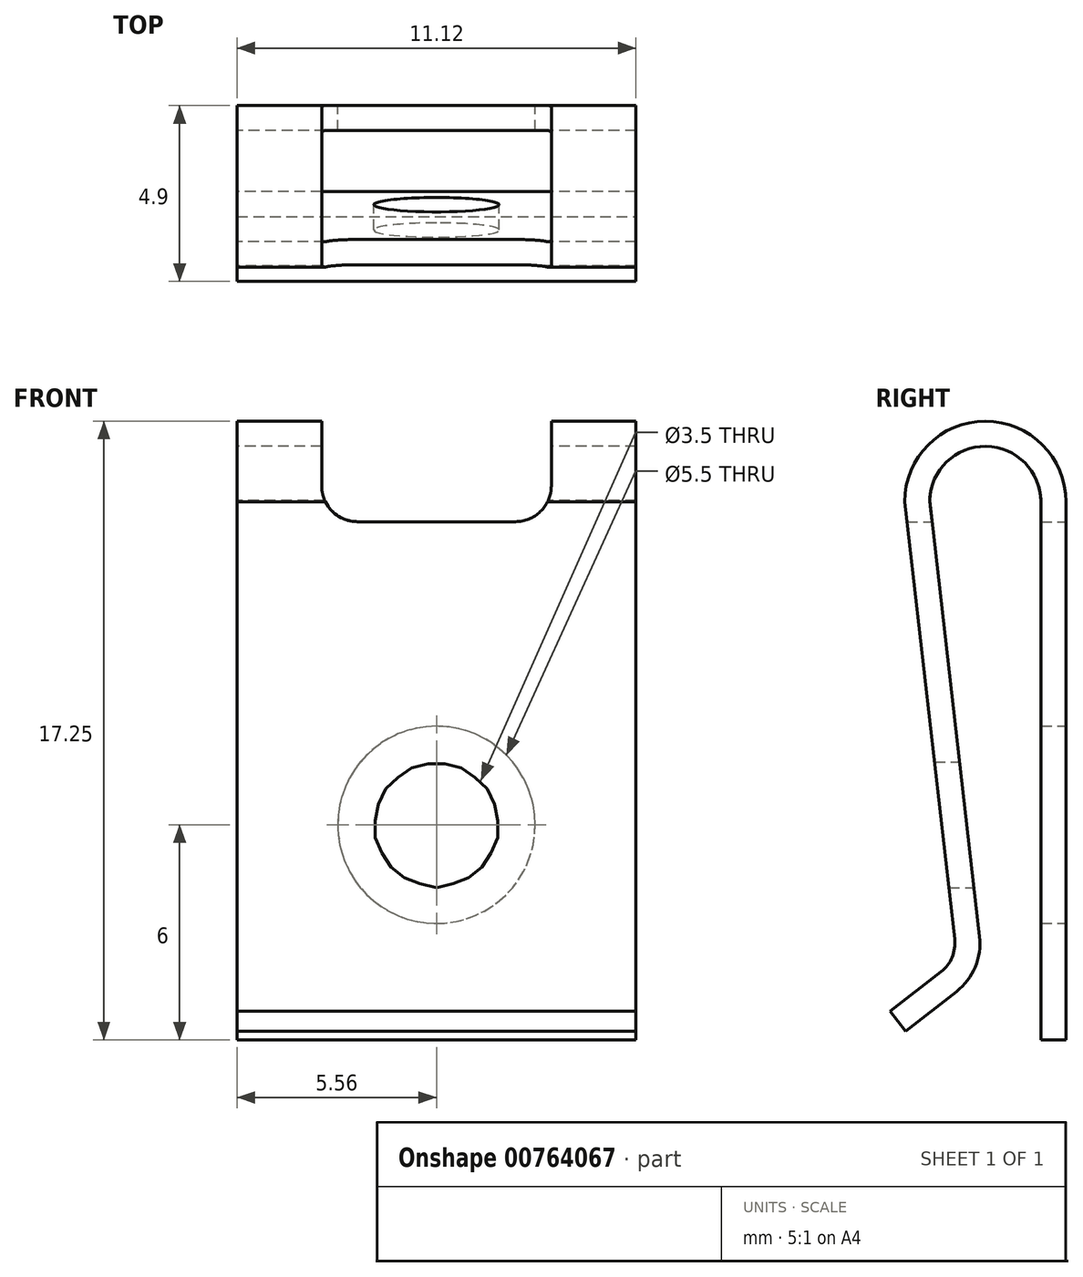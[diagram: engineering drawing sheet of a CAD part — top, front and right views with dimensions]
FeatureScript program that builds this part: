
annotation { "Feature Type Name" : "Feature", "Feature Type Description" : "" }
export const myFeature = defineFeature(function(context is Context, id is Id, definition is map)
    precondition{}
    {
        {
            var Q0;
            Q0=qCreatedBy(makeId("Right.planeOp"),FACE);
            var sketch = newSketch(context, id + "F0", { "sketchPlane" : qUnion([Q0])});
            skLineSegment(sketch, "E0", {"start": v(2.25, -15) * mm, "end": v(2.25, 0) * mm});
            skLineSegment(sketch, "E1", {"start": v(2.25, 0) * mm, "end": v(-2.25, 0) * mm, "construction": true});
            skLineSegment(sketch, "E2", {"start": v(-2.25, 0) * mm, "end": v(-0.8, -12.75) * mm});
            skLineSegment(sketch, "E3", {"start": v(-0.8, -12.75) * mm, "end": v(-2.65, -14.2) * mm});
            skArc(sketch, "E4", {"start": v(2.25, 0) * mm, "mid": v(0, 2.25) * mm, "end": v(-2.25, 0) * mm});
            skLineSegment(sketch, "E5.0", {"start": v(-0.05, -13.06) * mm, "end": v(-2.22, -14.75) * mm});
            skLineSegment(sketch, "E5.1", {"start": v(-1.55, 0.04) * mm, "end": v(-0.05, -13.06) * mm});
            skArc(sketch, "E5.2", {"start": v(1.55, 0) * mm, "mid": v(0.02, 1.55) * mm, "end": v(-1.55, 0.04) * mm});
            skLineSegment(sketch, "E5.3", {"start": v(1.55, -15) * mm, "end": v(1.55, 0) * mm});
            skLineSegment(sketch, "E6", {"start": v(-2.22, -14.75) * mm, "end": v(-2.65, -14.2) * mm});
            skLineSegment(sketch, "E7", {"start": v(2.25, -15) * mm, "end": v(1.55, -15) * mm});
            skSolve(sketch);
        }
        {
            var Q0;
            Q0=makeQuery(id+"F0.imprint","IMPRINT",FACE,{"disambiguationData":[TD([[makeQuery(id+"F0.imprint","IMPRINT",EDGE,{"derivedFrom":sQuery(id+"F0.wireOp",EDGE,"E0")}),1.0]])]});
            extrude(context, id + "F1", {"entities" : qUnion([Q0]), "endBound" : BoundingType.SYMMETRIC, "depth" : 11.12 * mm});
        }
        {
            var Q0;
            Q0=makeQuery(id+"F1.opExtrude","SWEPT_FACE",FACE,{"disambiguationData":[OSD([sQuery(id+"F0.wireOp",EDGE,"E0")])]});
            var sketch = newSketch(context, id + "F2", { "sketchPlane" : qUnion([Q0])});
            skLineSegment(sketch, "E8", {"start": v(0, -15) * mm, "end": v(0, -9) * mm, "construction": true});
            skCircle(sketch, "E9", {"center": v(0, -9) * mm, "radius": 2.75 * mm});
            skCircle(sketch, "E10", {"center": v(0, -9) * mm, "radius": 1.75 * mm});
            skLineSegment(sketch, "E11.bottom", {"start": v(-3.2, 3.95) * mm, "end": v(3.2, 3.95) * mm});
            skLineSegment(sketch, "E11.top", {"start": v(-3.2, -0.55) * mm, "end": v(3.2, -0.55) * mm});
            skLineSegment(sketch, "E11.left", {"start": v(-3.2, 3.95) * mm, "end": v(-3.2, -0.55) * mm});
            skLineSegment(sketch, "E11.right", {"start": v(3.2, 3.95) * mm, "end": v(3.2, -0.55) * mm});
            skSolve(sketch);
        }
        {
            var Q0;
            {var subQ0=sQuery(id+"F2.wireOp",EDGE,"E11.bottom");Q0=makeQuery(id+"F2.imprint","IMPRINT",FACE,{"disambiguationData":[TD([[makeQuery(id+"F2.imprint","IMPRINT",EDGE,{"derivedFrom":subQ0}),-1.0]])]});}
            var Q1;
            {var subQ0=sQuery(id+"F2.wireOp",EDGE,"E11.top");Q1=makeQuery(id+"F2.imprint","IMPRINT",FACE,{"disambiguationData":[TD([[makeQuery(id+"F2.imprint","IMPRINT",EDGE,{"derivedFrom":subQ0}),1.0]])]});}
            var Q2;
            Q2=makeQuery(id+"F2.imprint","IMPRINT",FACE,{"disambiguationData":[TD([[makeQuery(id+"F2.imprint","IMPRINT",EDGE,{"derivedFrom":sQuery(id+"F2.wireOp",EDGE,"E10")}),1.0]])]});
            extrude(context, id + "F3", {"entities" : qUnion([Q0, Q1, Q2]), "operationType" : NewBodyOperationType.REMOVE, "endBound" : BoundingType.THROUGH_ALL, "oppositeDirection" : true, "depth" : 25 * mm});
        }
        {
            var Q0;
            Q0=makeQuery(id+"F2.imprint","IMPRINT",FACE,{"disambiguationData":[TD([[makeQuery(id+"F2.imprint","IMPRINT",EDGE,{"derivedFrom":sQuery(id+"F2.wireOp",EDGE,"E9")}),1.0]])]});
            var Q1;
            Q1=makeQuery(id+"F1.opExtrude","SWEPT_FACE",FACE,{"disambiguationData":[OSD([sQuery(id+"F0.wireOp",EDGE,"E5.3")])]});
            extrude(context, id + "F4", {"entities" : qUnion([Q0]), "operationType" : NewBodyOperationType.REMOVE, "endBound" : BoundingType.UP_TO_SURFACE, "oppositeDirection" : true, "endBoundEntityFace" : qUnion([Q1]), "depth" : 25 * mm});
        }
        {
            var Q0;
            Q0=makeQuery(id+"F3.boolean.opBoolean","COPY",EDGE,{"disambiguationData":[OD(0.0)],"derivedFrom":makeQuery(id+"F3.opExtrude","SWEPT_EDGE",EDGE,{"disambiguationData":[OSD([sQuery(id+"F2.wireOp",EDGE,"E11.top"),sQuery(id+"F2.wireOp",EDGE,"E11.right")])]})});
            var Q1;
            Q1=makeQuery(id+"F3.boolean.opBoolean","COPY",EDGE,{"disambiguationData":[OD(1.0)],"derivedFrom":makeQuery(id+"F3.opExtrude","SWEPT_EDGE",EDGE,{"disambiguationData":[OSD([sQuery(id+"F2.wireOp",EDGE,"E11.top"),sQuery(id+"F2.wireOp",EDGE,"E11.right")])]})});
            var Q2;
            Q2=makeQuery(id+"F3.boolean.opBoolean","COPY",EDGE,{"disambiguationData":[OD(0.0)],"derivedFrom":makeQuery(id+"F3.opExtrude","SWEPT_EDGE",EDGE,{"disambiguationData":[OSD([sQuery(id+"F2.wireOp",EDGE,"E11.top"),sQuery(id+"F2.wireOp",EDGE,"E11.left")])]})});
            var Q3;
            Q3=makeQuery(id+"F3.boolean.opBoolean","COPY",EDGE,{"disambiguationData":[OD(1.0)],"derivedFrom":makeQuery(id+"F3.opExtrude","SWEPT_EDGE",EDGE,{"disambiguationData":[OSD([sQuery(id+"F2.wireOp",EDGE,"E11.top"),sQuery(id+"F2.wireOp",EDGE,"E11.left")])]})});
            var Q4;
            Q4=makeQuery(id+"F1.opExtrude","SWEPT_EDGE",EDGE,{"disambiguationData":[OSD([sQuery(id+"F0.wireOp",EDGE,"E2"),sQuery(id+"F0.wireOp",EDGE,"E3")])]});
            fillet(context, id + "F5", {"entities" : qUnion([Q0, Q1, Q2, Q3, Q4]), "radius" : 1 * mm, "tangentPropagation" : true, "allowEdgeOverflow" : false});
        }
        {
            var Q0;
            Q0=makeQuery(id+"F1.opExtrude","SWEPT_EDGE",EDGE,{"disambiguationData":[OSD([sQuery(id+"F0.wireOp",EDGE,"E5.0"),sQuery(id+"F0.wireOp",EDGE,"E5.1")])]});
            fillet(context, id + "F6", {"entities" : qUnion([Q0]), "radius" : 1.7 * mm, "tangentPropagation" : true, "allowEdgeOverflow" : false});
        }
    });
